# Revit family: Sink-Bradley_Corp-Verge_LVSD2
name_source: partatom
category: Plumbing Fixtures
revit_build: Autodesk Revit 2013 (Build: 20120221_2030(x64)
units: mm (PartAtom-declared; Revit-internal decimal feet)

## types (1)
- LVSD2
    ADA Compliant = Yes
    Access Panel Material = Metal - Bradley Corp - Stainless Steel
    Apparent Load = 0 VA
    Assembly Code = D2010400
    CWFU = 0.5
    Cold Water Connection Diameter = 0.5 "
    Cold Water Connection Radius = 0.25 "
    Depth = 21 "
    Description = Verge™ Lavatory System – VLS Series, Two-Station
    Evero™ Bowl Material = Stone - Bradley Corp - Antarctica
    Fixture Material = Metal - Bradley Corp - Chrome
    HWFU = 0.5
    Height = 33.5 "
    Hot Water Connection Diameter = 0.5 "
    Hot Water Connection Radius = 0.25 "
    Industry Standards = ANSI Z124.3, ANSI Z124.6, ANSI/OCPA SS-1-2001, UPC, GREENGUARD Indoor Air Quality Certified®, GREENGUARD Children & Schools(SM)
    Installation Type = Wall Mounted
    Low Emitting Material = Yes
    Manufacturer = Bradley Corporation
    Manufacturer Installation URL - English = https://www.bradleycorp.com
    MasterFormat Number = 22 42 16
    MasterFormat Title = Commercial Lavatories and Sinks
    Material = Polyester Resin
    Material Note = Other Evero® colors available - See www.bradleycorp.com
    Model = LVSD2
    Number of Poles = 1
    OmniClass Table 21 Number = 21-04 20 10 60
    OmniClass Table 21 Title = Plumbing Fixtures
    OmniClass Table 23 Number = 23-31 13 00
    OmniClass Table 23 Title = Sink/Lavatories
    Pedestal Width = 36 "
    Percentage of Recycled Content = 0
    Power Factor = 1
    Product Tech Data URL - English = https://www.bradleycorp.com
    Specifications URL = http://www.bradleycorp.com
    URL = http://www.bradleycorp.com
    Version = 3.0
    Voltage = 110 V
    WFU = 1.5
    Waste Connection Diameter = 1.5 "
    Waste Connection Radius = 0.75 "
    Width = 60 "

## geometry (parser evidence)
native form markers: Blend x48, Sweep x3
no freeform markers — native parametric forms only
